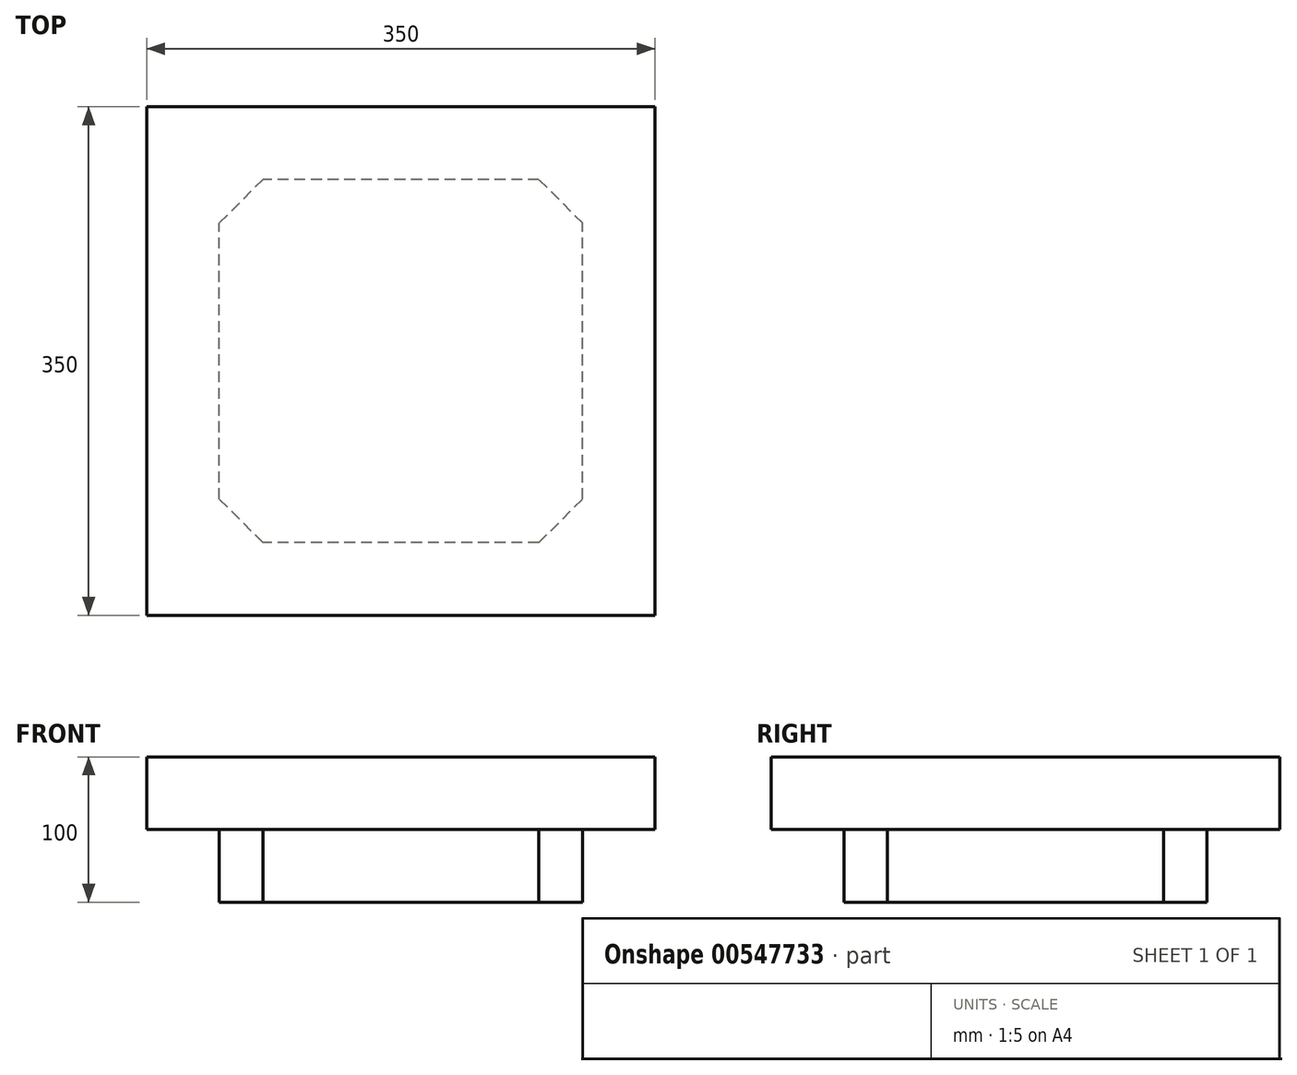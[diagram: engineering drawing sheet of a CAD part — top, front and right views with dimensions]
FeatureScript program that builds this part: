
annotation { "Feature Type Name" : "Feature", "Feature Type Description" : "" }
export const myFeature = defineFeature(function(context is Context, id is Id, definition is map)
    precondition{}
    {
        {
            var Q0;
            Q0=qCreatedBy(makeId("Top.planeOp"),FACE);
            var sketch = newSketch(context, id + "F0", { "sketchPlane" : qUnion([Q0])});
            skLineSegment(sketch, "E0.bottom", {"start": v(175, 175) * mm, "end": v(-175, 175) * mm});
            skLineSegment(sketch, "E0.top", {"start": v(175, -175) * mm, "end": v(-175, -175) * mm});
            skLineSegment(sketch, "E0.left", {"start": v(175, 175) * mm, "end": v(175, -175) * mm});
            skLineSegment(sketch, "E0.right", {"start": v(-175, 175) * mm, "end": v(-175, -175) * mm});
            skPoint(sketch, "E0.middle", {"position": v(0, 0) * mm});
            skSolve(sketch);
        }
        {
            var Q0;
            Q0=qSketchRegion(id+"F0",true);
            extrude(context, id + "F1", {"entities" : qUnion([Q0]), "depth" : 50 * mm, "offsetDistance" : 25 * mm});
        }
        {
            var Q0;
            Q0=qCreatedBy(makeId("Top.planeOp"),FACE);
            var sketch = newSketch(context, id + "F2", { "sketchPlane" : qUnion([Q0])});
            skLineSegment(sketch, "E1.bottom", {"start": v(95, -125) * mm, "end": v(-95, -125) * mm});
            skLineSegment(sketch, "E1.top", {"start": v(95, 125) * mm, "end": v(-95, 125) * mm});
            skLineSegment(sketch, "E1.left", {"start": v(125, -95) * mm, "end": v(125, 95) * mm});
            skLineSegment(sketch, "E1.right", {"start": v(-125, -95) * mm, "end": v(-125, 95) * mm});
            skPoint(sketch, "E1.middle", {"position": v(0, 0) * mm});
            skLineSegment(sketch, "E2", {"start": v(-95, -125) * mm, "end": v(-125, -95) * mm});
            skLineSegment(sketch, "E3", {"start": v(-95, 125) * mm, "end": v(-125, 95) * mm});
            skLineSegment(sketch, "E4", {"start": v(125, 95) * mm, "end": v(95, 125) * mm});
            skLineSegment(sketch, "E5", {"start": v(95, -125) * mm, "end": v(125, -95) * mm});
            skPoint(sketch, "E6.orphan", {"position": v(-125, -125) * mm});
            skPoint(sketch, "E7.orphan", {"position": v(125, -125) * mm});
            skPoint(sketch, "E8.orphan", {"position": v(125, 125) * mm});
            skPoint(sketch, "E9.orphan", {"position": v(-125, 125) * mm});
            skSolve(sketch);
        }
        {
            var Q0;
            Q0=qSketchRegion(id+"F2",true);
            extrude(context, id + "F3", {"entities" : qUnion([Q0]), "operationType" : NewBodyOperationType.ADD, "oppositeDirection" : true, "depth" : 50 * mm, "offsetDistance" : 25 * mm});
        }
    });
